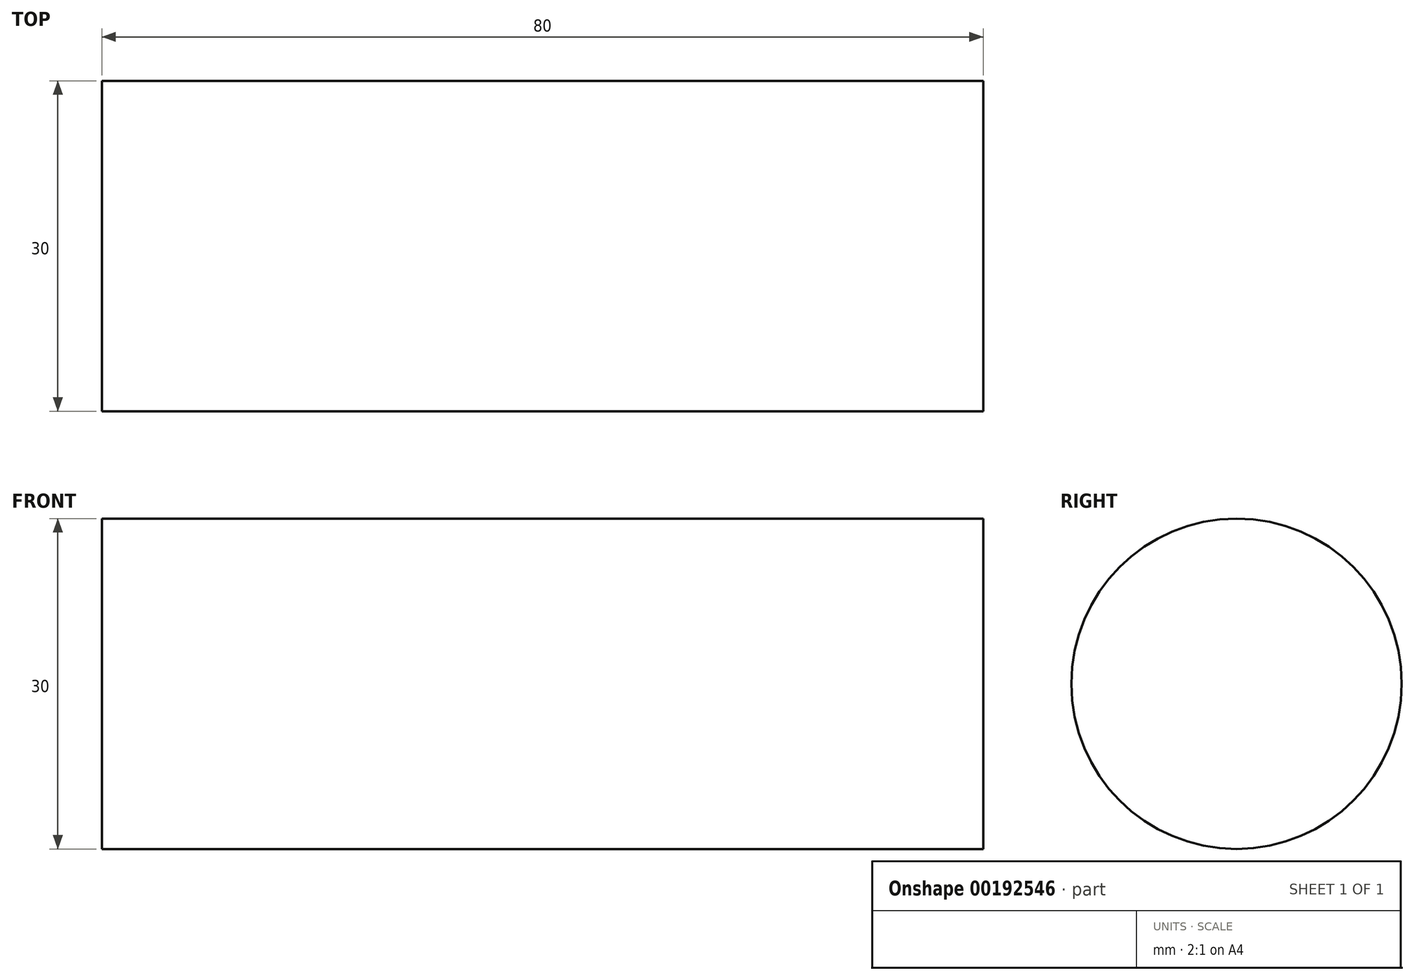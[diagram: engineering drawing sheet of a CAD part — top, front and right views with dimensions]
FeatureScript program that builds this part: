
annotation { "Feature Type Name" : "Feature", "Feature Type Description" : "" }
export const myFeature = defineFeature(function(context is Context, id is Id, definition is map)
    precondition{}
    {
        {
            var Q0;
            Q0=qCreatedBy(makeId("Right.planeOp"),FACE);
            var sketch = newSketch(context, id + "F0", { "sketchPlane" : qUnion([Q0])});
            skCircle(sketch, "E0", {"center": v(0, 0) * mm, "radius": 15 * mm});
            skSolve(sketch);
        }
        {
            var Q0;
            Q0 = qSketchRegion(id + "F0", true);
            extrude(context, id + "F1", {"entities" : qUnion([Q0]), "depth" : 80 * mm});
        }
    });
